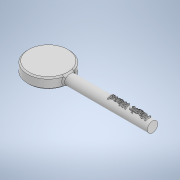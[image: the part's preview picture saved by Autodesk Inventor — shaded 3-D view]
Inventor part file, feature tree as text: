
AUTODESK INVENTOR PART (.ipt)
format: ipt  version: 2020 (Build 240168000, 168)  size: 510,976 bytes
history: native  units: in
note: dims shown in document units (in); Inventor stores cm internally (conversion verified against a paired STEP export)
features: sketch x3, extrude x2, chamfer x1, emboss x1
ambient origin geometry x8: Origin, YZ Plane, XZ Plane, XY Plane, X Axis, Y Axis, Z Axis, Center Point
bodies: Solid1 (feature_tree)
feature tree (7):
  extrude  "Extrusion1"  Depth=0.5in TaperAngle=0.0deg
  extrude  "Extrusion2"  Depth=0.0625in TaperAngle=45.0deg
  chamfer  "Chamfer1"  Distance=0.0625in
  emboss  "Emboss1"
  sketch  "Sketch1"  dims[d0=2.0in d1=0.5in d2=0.0in]
  sketch  "Sketch2"  dims[d3=5.0in d4=0.0in d5=0.0625in d6=0.125in d7=45.0deg d8=0.0625in d9=0.0in]
  sketch  "Sketch3"
